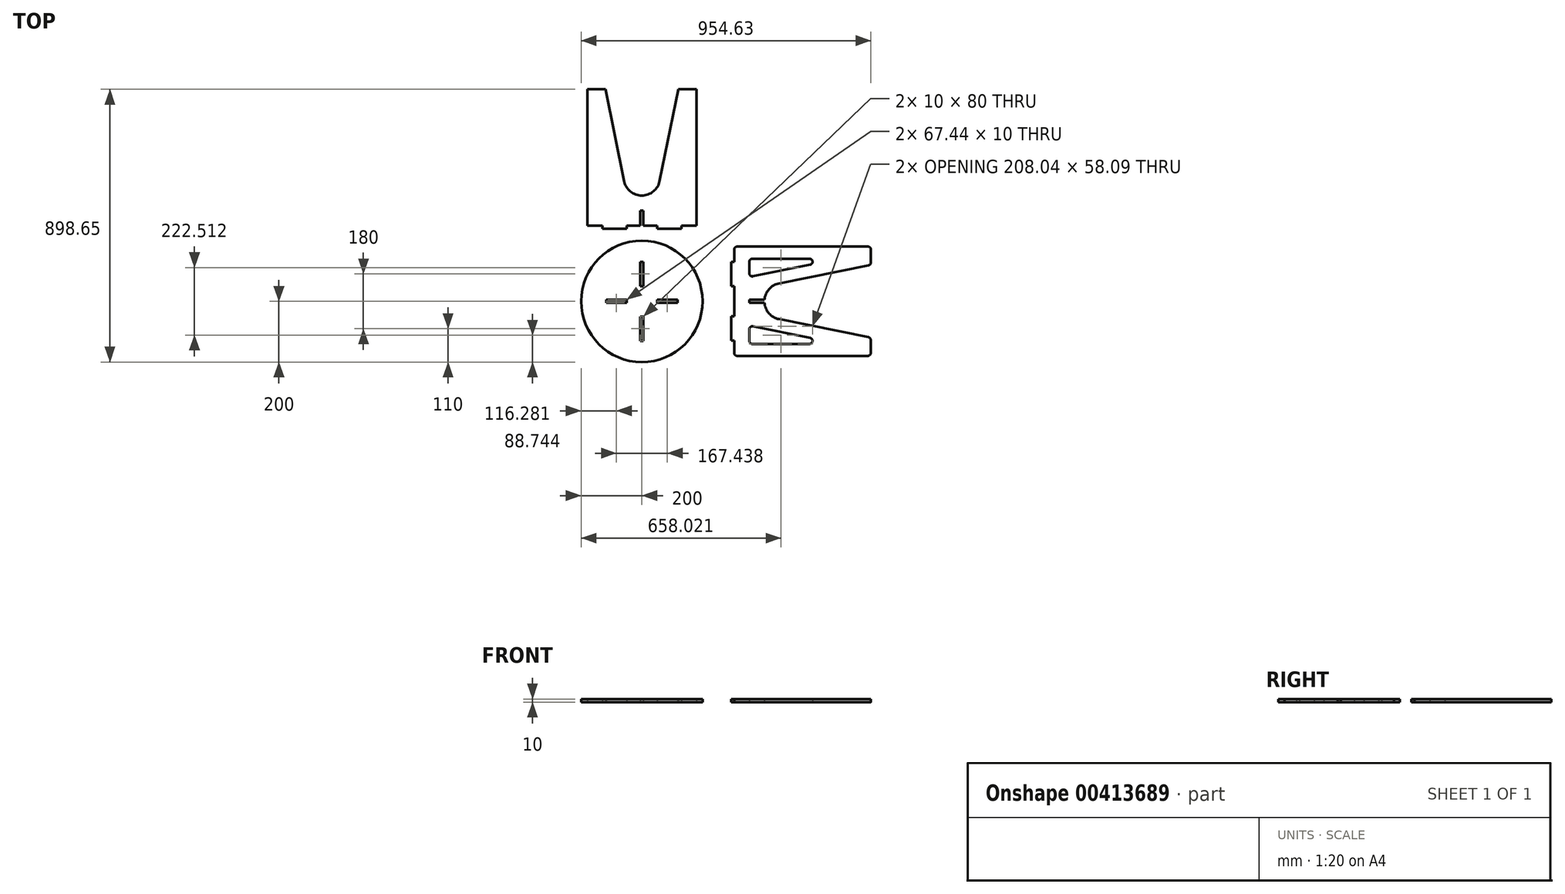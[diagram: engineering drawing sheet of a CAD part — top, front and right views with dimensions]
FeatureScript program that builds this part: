
annotation { "Feature Type Name" : "Feature", "Feature Type Description" : "" }
export const myFeature = defineFeature(function(context is Context, id is Id, definition is map)
    precondition{}
    {
        {
            var Q0;
            Q0=qCreatedBy(makeId("Top.planeOp"),FACE);
            var sketch = newSketch(context, id + "F0", { "sketchPlane" : qUnion([Q0])});
            skCircle(sketch, "E0", {"center": v(0, 0) * mm, "radius": 200 * mm});
            skLineSegment(sketch, "E1.bottom", {"start": v(-5, 130) * mm, "end": v(5, 130) * mm});
            skLineSegment(sketch, "E1.top", {"start": v(-5, 50) * mm, "end": v(5, 50) * mm});
            skLineSegment(sketch, "E1.left", {"start": v(-5, 130) * mm, "end": v(-5, 50) * mm});
            skLineSegment(sketch, "E1.right", {"start": v(5, 130) * mm, "end": v(5, 50) * mm});
            skLineSegment(sketch, "E2.MirrorCS", {"start": v(-5, -50) * mm, "end": v(5, -50) * mm});
            skLineSegment(sketch, "E3.MirrorCS", {"start": v(-5, -130) * mm, "end": v(5, -130) * mm});
            skLineSegment(sketch, "E4.MirrorCS", {"start": v(5, -130) * mm, "end": v(5, -50) * mm});
            skLineSegment(sketch, "E5.MirrorCS", {"start": v(-5, -130) * mm, "end": v(-5, -50) * mm});
            skLineSegment(sketch, "E6.MirrorCS", {"start": v(-117.44, -5) * mm, "end": v(-117.44, 5) * mm});
            skLineSegment(sketch, "E7.MirrorCS", {"start": v(-50, -5) * mm, "end": v(-50, 5) * mm});
            skLineSegment(sketch, "E8.MirrorCS", {"start": v(-50, 5) * mm, "end": v(-117.44, 5) * mm});
            skLineSegment(sketch, "E9.MirrorCS", {"start": v(-50, -5) * mm, "end": v(-117.44, -5) * mm});
            skLineSegment(sketch, "E10.MirrorCS", {"start": v(117.44, -5) * mm, "end": v(117.44, 5) * mm});
            skLineSegment(sketch, "E11.MirrorCS", {"start": v(50, 5) * mm, "end": v(117.44, 5) * mm});
            skLineSegment(sketch, "E12.MirrorCS", {"start": v(50, -5) * mm, "end": v(117.44, -5) * mm});
            skLineSegment(sketch, "E13.MirrorCS", {"start": v(50, -5) * mm, "end": v(50, 5) * mm});
            skLineSegment(sketch, "E14", {"start": v(-180, 248.65) * mm, "end": v(-130, 248.65) * mm});
            skLineSegment(sketch, "E15", {"start": v(180, 248.65) * mm, "end": v(180, 698.65) * mm});
            skLineSegment(sketch, "E16", {"start": v(180, 698.65) * mm, "end": v(120, 698.65) * mm});
            skLineSegment(sketch, "E17", {"start": v(120, 698.65) * mm, "end": v(58.8, 396.73) * mm});
            skLineSegment(sketch, "E18", {"start": v(130, 248.65) * mm, "end": v(130, 238.65) * mm});
            skLineSegment(sketch, "E19", {"start": v(130, 238.65) * mm, "end": v(50, 238.65) * mm});
            skLineSegment(sketch, "E20", {"start": v(50, 238.65) * mm, "end": v(50, 248.65) * mm});
            skLineSegment(sketch, "E21.trimOffspring", {"start": v(130, 248.65) * mm, "end": v(180, 248.65) * mm});
            skLineSegment(sketch, "E22.MirrorCS", {"start": v(-130, 248.65) * mm, "end": v(-130, 238.65) * mm});
            skLineSegment(sketch, "E23.MirrorCS", {"start": v(-50, 238.65) * mm, "end": v(-50, 248.65) * mm});
            skLineSegment(sketch, "E24.MirrorCS", {"start": v(-130, 238.65) * mm, "end": v(-50, 238.65) * mm});
            skLineSegment(sketch, "E25.MirrorCS", {"start": v(-180, 698.65) * mm, "end": v(-120, 698.65) * mm});
            skLineSegment(sketch, "E26.MirrorCS", {"start": v(-120, 698.65) * mm, "end": v(-58.8, 396.73) * mm});
            skLineSegment(sketch, "E27.trimOffspring", {"start": v(-50, 248.65) * mm, "end": v(-5, 248.65) * mm});
            skLineSegment(sketch, "E28", {"start": v(-180, 248.65) * mm, "end": v(-180, 698.65) * mm});
            skPoint(sketch, "E29.newPointA", {"position": v(-50, 353.3) * mm});
            skPoint(sketch, "E29.newPointB", {"position": v(50, 353.3) * mm});
            skArc(sketch, "E29.filletArc", {"start": v(-58.8, 396.73) * mm, "mid": v(0, 348.65) * mm, "end": v(58.8, 396.73) * mm});
            skLineSegment(sketch, "E30.bottom", {"start": v(-5, 298.65) * mm, "end": v(5, 298.65) * mm});
            skLineSegment(sketch, "E30.left", {"start": v(-5, 298.65) * mm, "end": v(-5, 248.65) * mm});
            skLineSegment(sketch, "E30.right", {"start": v(5, 298.65) * mm, "end": v(5, 248.65) * mm});
            skLineSegment(sketch, "E31.trimOffspring", {"start": v(5, 248.65) * mm, "end": v(50, 248.65) * mm});
            skLineSegment(sketch, "E32", {"start": v(304, 170.3) * mm, "end": v(304, 130.3) * mm});
            skLineSegment(sketch, "E33", {"start": v(314, -179.7) * mm, "end": v(744, -179.7) * mm});
            skLineSegment(sketch, "E34", {"start": v(754, -169.7) * mm, "end": v(754, -127.88) * mm});
            skLineSegment(sketch, "E35", {"start": v(745.98, -118.08) * mm, "end": v(451.7, -58.67) * mm});
            skLineSegment(sketch, "E36", {"start": v(304, -129.7) * mm, "end": v(294, -129.7) * mm});
            skLineSegment(sketch, "E37", {"start": v(294, -129.7) * mm, "end": v(294, -49.7) * mm});
            skLineSegment(sketch, "E38", {"start": v(294, -49.7) * mm, "end": v(304, -49.7) * mm});
            skLineSegment(sketch, "E39.trimOffspring", {"start": v(304, -129.7) * mm, "end": v(304, -169.7) * mm});
            skLineSegment(sketch, "E40.MirrorCS", {"start": v(304, 130.3) * mm, "end": v(294, 130.3) * mm});
            skLineSegment(sketch, "E41.MirrorCS", {"start": v(294, 50.3) * mm, "end": v(304, 50.3) * mm});
            skLineSegment(sketch, "E42.MirrorCS", {"start": v(294, 130.3) * mm, "end": v(294, 50.3) * mm});
            skLineSegment(sketch, "E43.MirrorCS", {"start": v(754.63, 170.3) * mm, "end": v(754.63, 128.48) * mm});
            skLineSegment(sketch, "E44.MirrorCS", {"start": v(746.61, 118.68) * mm, "end": v(451.67, 58.95) * mm});
            skLineSegment(sketch, "E45", {"start": v(314, 180.3) * mm, "end": v(744.63, 180.3) * mm});
            skPoint(sketch, "E46.newPointA", {"position": v(409.36, 50.38) * mm});
            skPoint(sketch, "E46.newPointB", {"position": v(407.26, -49.7) * mm});
            skArc(sketch, "E46.filletArc", {"start": v(451.67, 58.95) * mm, "mid": v(418.75, 40.03) * mm, "end": v(403.78, 5.14) * mm});
            skLineSegment(sketch, "E47.bottom", {"start": v(-262.6, 711.4) * mm, "end": v(-252.6, 711.4) * mm});
            skLineSegment(sketch, "E48", {"start": v(353.78, 5.12) * mm, "end": v(353.8, -4.88) * mm});
            skLineSegment(sketch, "E49.MirrorCS", {"start": v(353.78, 5.12) * mm, "end": v(403.78, 5.14) * mm});
            skLineSegment(sketch, "E50.MirrorCS", {"start": v(353.8, -4.88) * mm, "end": v(403.79, -4.86) * mm});
            skArc(sketch, "E51.trimOffspring", {"start": v(403.79, -4.86) * mm, "mid": v(418.77, -39.76) * mm, "end": v(451.7, -58.67) * mm});
            skLineSegment(sketch, "E52", {"start": v(304, 50.3) * mm, "end": v(304, -49.7) * mm});
            skLineSegment(sketch, "E53.0", {"start": v(364, 140.3) * mm, "end": v(552.1, 140.3) * mm});
            skLineSegment(sketch, "E54.0", {"start": v(354, 130.3) * mm, "end": v(354, 92.2) * mm});
            skPoint(sketch, "E55.visualSharp", {"position": v(354, 79.98) * mm});
            skArc(sketch, "E55.filletArc", {"start": v(354, 92.2) * mm, "mid": v(357.67, 84.47) * mm, "end": v(365.98, 82.4) * mm});
            skPoint(sketch, "E56.visualSharp", {"position": v(354, 140.3) * mm});
            skArc(sketch, "E56.filletArc", {"start": v(364, 140.3) * mm, "mid": v(356.93, 137.37) * mm, "end": v(354, 130.3) * mm});
            skPoint(sketch, "E57.visualSharp", {"position": v(651.86, 140.3) * mm});
            skArc(sketch, "E57.filletArc", {"start": v(554.08, 120.5) * mm, "mid": v(562.04, 131.3) * mm, "end": v(552.1, 140.3) * mm});
            skPoint(sketch, "E58.visualSharp", {"position": v(304, 180.3) * mm});
            skArc(sketch, "E58.filletArc", {"start": v(314, 180.3) * mm, "mid": v(306.93, 177.37) * mm, "end": v(304, 170.3) * mm});
            skPoint(sketch, "E59.visualSharp", {"position": v(754.63, 180.3) * mm});
            skArc(sketch, "E59.filletArc", {"start": v(754.63, 170.3) * mm, "mid": v(751.7, 177.37) * mm, "end": v(744.63, 180.3) * mm});
            skPoint(sketch, "E60.visualSharp", {"position": v(754.63, 120.3) * mm});
            skArc(sketch, "E60.filletArc", {"start": v(746.61, 118.68) * mm, "mid": v(752.37, 122.15) * mm, "end": v(754.63, 128.48) * mm});
            skPoint(sketch, "E61.visualSharp", {"position": v(304, -179.7) * mm});
            skArc(sketch, "E61.filletArc", {"start": v(304, -169.7) * mm, "mid": v(306.93, -176.77) * mm, "end": v(314, -179.7) * mm});
            skPoint(sketch, "E62.visualSharp", {"position": v(754, -119.7) * mm});
            skArc(sketch, "E62.filletArc", {"start": v(754, -127.88) * mm, "mid": v(751.74, -121.55) * mm, "end": v(745.98, -118.08) * mm});
            skPoint(sketch, "E63.visualSharp", {"position": v(754, -179.7) * mm});
            skArc(sketch, "E63.filletArc", {"start": v(744, -179.7) * mm, "mid": v(751.07, -176.77) * mm, "end": v(754, -169.7) * mm});
            skLineSegment(sketch, "E64", {"start": v(365.98, 82.4) * mm, "end": v(554.08, 120.5) * mm});
            skArc(sketch, "E65.MirrorCS", {"start": v(354, -92.2) * mm, "mid": v(357.67, -84.47) * mm, "end": v(365.98, -82.4) * mm});
            skArc(sketch, "E66.MirrorCS", {"start": v(364, -140.3) * mm, "mid": v(356.93, -137.37) * mm, "end": v(354, -130.3) * mm});
            skLineSegment(sketch, "E67.MirrorCS", {"start": v(364, -140.3) * mm, "end": v(552.1, -140.3) * mm});
            skPoint(sketch, "E68.MirrorP", {"position": v(354, -140.3) * mm});
            skLineSegment(sketch, "E69.MirrorCS", {"start": v(365.98, -82.4) * mm, "end": v(554.08, -120.5) * mm});
            skLineSegment(sketch, "E70.MirrorCS", {"start": v(354, -130.3) * mm, "end": v(354, -92.2) * mm});
            skArc(sketch, "E71.MirrorCS", {"start": v(554.08, -120.5) * mm, "mid": v(562.04, -131.3) * mm, "end": v(552.1, -140.3) * mm});
            skSolve(sketch);
        }
        {
            var Q0;
            Q0 = qSketchRegion(id + "F0", true);
            extrude(context, id + "F1", {"entities" : qUnion([Q0]), "depth" : 10 * mm});
        }
    });
